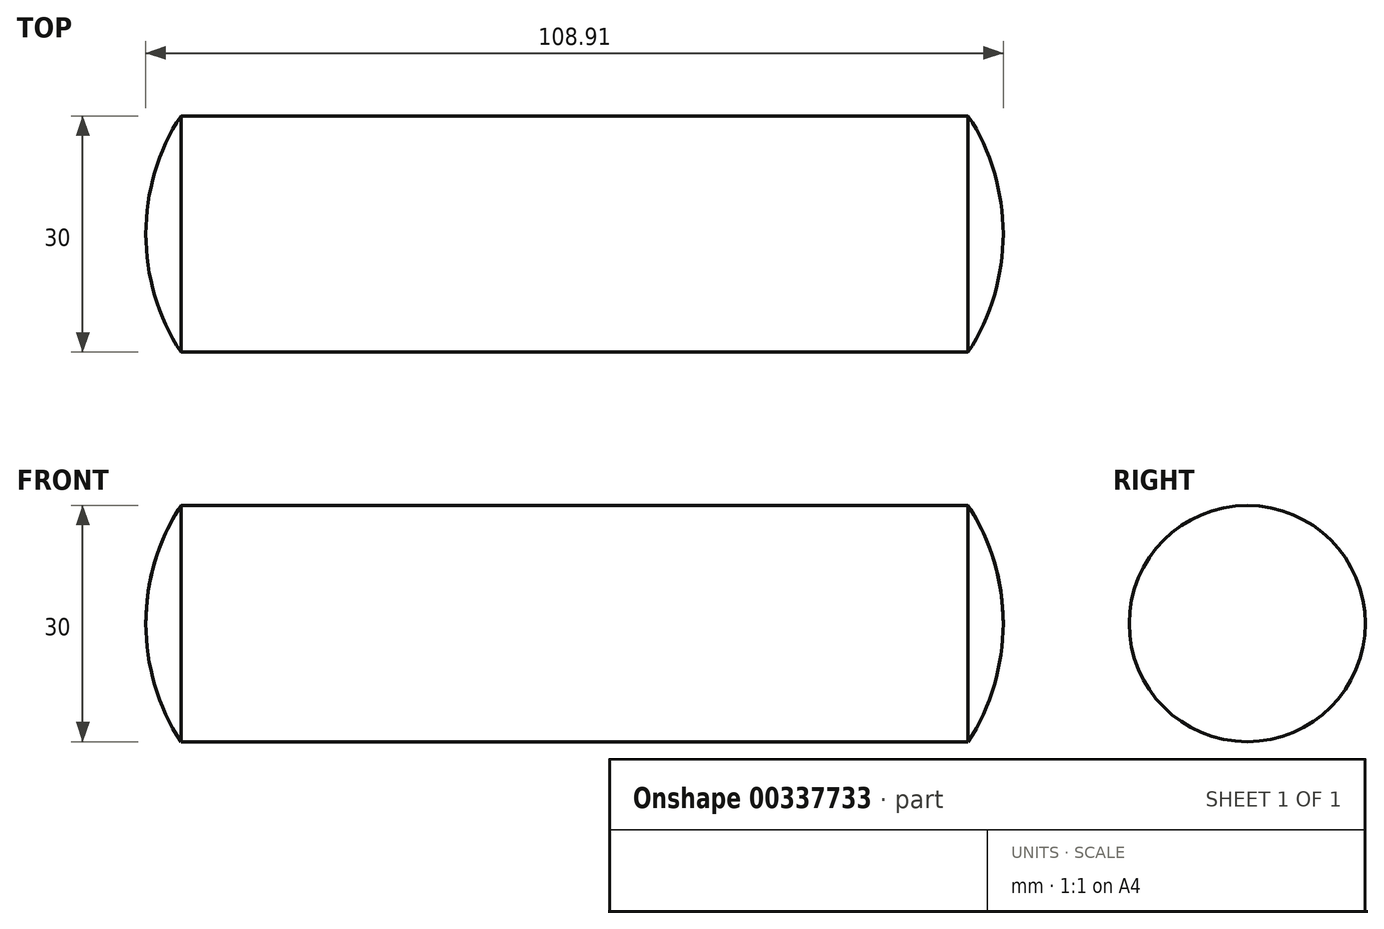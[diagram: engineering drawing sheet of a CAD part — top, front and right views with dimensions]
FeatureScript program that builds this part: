
annotation { "Feature Type Name" : "Feature", "Feature Type Description" : "" }
export const myFeature = defineFeature(function(context is Context, id is Id, definition is map)
    precondition{}
    {
        {
            var Q0;
            Q0=qCreatedBy(makeId("Front.planeOp"),FACE);
            var sketch = newSketch(context, id + "F0", { "sketchPlane" : qUnion([Q0])});
            skLineSegment(sketch, "E0", {"start": v(63.56, 15) * mm, "end": v(-36.44, 15) * mm});
            skLineSegment(sketch, "E1", {"start": v(-40.9, 0) * mm, "end": v(68, 0) * mm});
            skArc(sketch, "E2", {"start": v(-36.44, 15) * mm, "mid": v(-39.76, 7.82) * mm, "end": v(-40.9, 0) * mm});
            skArc(sketch, "E3", {"start": v(68, 0) * mm, "mid": v(66.87, 7.82) * mm, "end": v(63.56, 15) * mm});
            skLineSegment(sketch, "E4", {"start": v(-40.9, 0) * mm, "end": v(-40.9, 54.45) * mm});
            skLineSegment(sketch, "E5", {"start": v(68, 0) * mm, "end": v(68, 47.28) * mm});
            skSolve(sketch);
        }
        {
            var Q0;
            Q0=makeQuery(id+"F0.imprint","IMPRINT",FACE,{"disambiguationData":[TD([[makeQuery(id+"F0.imprint","IMPRINT",EDGE,{"derivedFrom":sQuery(id+"F0.wireOp",EDGE,"E0")}),1.0]])]});
            var Q1;
            Q1=sQuery(id+"F0.wireOp",EDGE,"E1");
            revolve(context, id + "F1", {"entities" : qUnion([Q0]), "axis" : qUnion([Q1]), "revolveType" : RevolveType.FULL});
        }
    });
